# Revit family: Domotics-DomesticRanges-GEWISS-CHORUS_POWER-SOCKET-OUTLET_DEU_COVER
name_source: partatom
category: Apparecchi elettrici
revit_build: Autodesk Revit 2016 (Build: 20161004_0715(x64)
units: mm (PartAtom-declared; Revit-internal decimal feet)

## family parameters
Condiviso = Sì
Host = Superficie
Mantenere orientamento annotazione = Sì
Punto di calcolo locali = Sì
Quota connettore circolare = Usa diametro
Taglio con vuoti quando caricato = Sì
Tipo di parte = Normale

## types (3) — shared parameters
Breaking capacity: = 1.25 In (100 position changes)
Carico apparente = 0 VA
Catalogue = DOMOTICS
Catalogue Range = CHORUS - DOMESTIC RANGE
Category = Socket-outlet
Characteristics = With safety shields
Description. = Socket-outlet
Description: = 2P+E - 16A
Electrocod = 0131
For plug pins = Ã˜ 4.8 mm
Glow Wire Test = 850°C
IDF = 6a066b17-f56b-4c47-b854-df18297a964e
IDT = df24d3f5-b374-4564-a63a-03cc912ed6d1
IP degree = IP40
Immagine tipo = GW14241.jpg
Insulation resistance = > 5 MOhm
N. poli = 1
No. Chorus modules = 2
No. Chorus modules: = 2
Produttore = GEWISS S.p.A.
Prolonged operation (no.of position changes) = 10.000 at In 250 V ac cosÃ˜=0,8
Prospetto di default = 1219 mm
Resistance at test voltage = 2000 V at 50 Hz for 1 minute
SEO = Socket outlet
Standard = German
Standard: = German
Standard; = IEC 60884-1; DIN VDE 0620-1
TXT ELETTRICO = 16
Technical sheet = https://www.gewiss.com
Terminal grip on cable traction = > 50 N
Terminal tightening capacity flexible cables (mm2) = min. 0,75 - max. 2x4
Terminal tightening capacity rigid cables (mm2) = min. 0,5 - max. 2x2,5
Thermo-pressure with ball = 125
Tipo_ = Chorus Prese Ger_GENERICO : GW14241 Presa 2M 2P+T 16A standard Tedesco titanio
URL = https://www.gewiss.com
Version file RFA = 19.0
Volt = 230 V
Voltage = 250 V ac
Voltage: = 250 V ac
Wiring terminals = With screw

## per-type parameters (varying)
| type | Colour | Descrizione | EAN code | Modello |
| GW10242 - Socket outlet Deu std 2M 2P+E 16A with cover white | White | DEU STD S.-OUT 2M 2P+E 16A WITH COVER WH | 8011564842021 | GW10242 |
| GW14242 - Socket outlet Deu std 2M 2P+E 16A with cover titanium | Titanium | DEU STD S.-OUT 2M 2P+E 16A WITH COVER TI | 8011564842045 | GW14242 |
| GW12242 - Socket outlet Deu std 2M 2P+E 16A with cover black | Black | DEU STD S.-OUT 2M 2P+E 16A WITH COVER BL | 8011564842038 | GW12242 |

note: source unit labels omitted for Thermo-pressure with ball — the stored unit's dimension contradicts the parameter name (converter mislabeling)

## geometry (parser evidence)
native form markers: Sweep x2
no freeform markers — native parametric forms only
